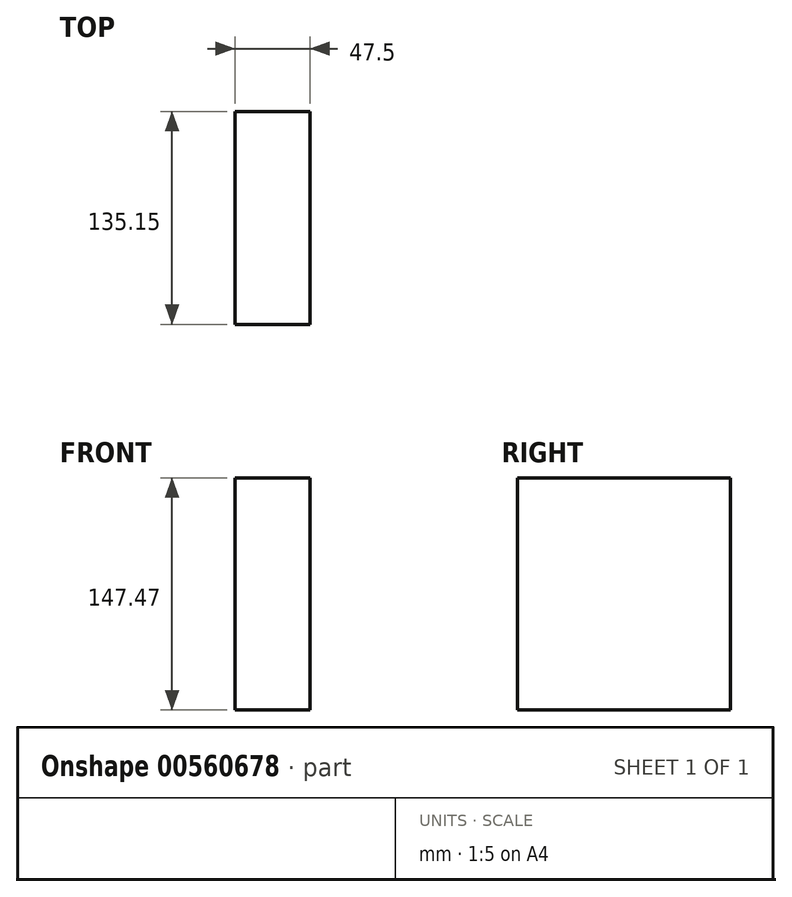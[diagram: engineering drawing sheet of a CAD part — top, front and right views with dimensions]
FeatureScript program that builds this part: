
annotation { "Feature Type Name" : "Feature", "Feature Type Description" : "" }
export const myFeature = defineFeature(function(context is Context, id is Id, definition is map)
    precondition{}
    {
        {
            var Q0;
            Q0=qCreatedBy(makeId("Right.planeOp"),FACE);
            var sketch = newSketch(context, id + "F0", { "sketchPlane" : qUnion([Q0])});
            skLineSegment(sketch, "E0.bottom", {"start": v(-32.49, 44.94) * mm, "end": v(102.66, 44.94) * mm});
            skLineSegment(sketch, "E0.top", {"start": v(-32.49, -102.53) * mm, "end": v(102.66, -102.53) * mm});
            skLineSegment(sketch, "E0.left", {"start": v(-32.49, 44.94) * mm, "end": v(-32.49, -102.53) * mm});
            skLineSegment(sketch, "E0.right", {"start": v(102.66, 44.94) * mm, "end": v(102.66, -102.53) * mm});
            skLineSegment(sketch, "E1.bottom", {"start": v(102.66, -102.53) * mm, "end": v(157.89, -102.53) * mm});
            skLineSegment(sketch, "E1.top", {"start": v(102.66, -130.9) * mm, "end": v(157.89, -130.9) * mm});
            skLineSegment(sketch, "E1.left", {"start": v(102.66, -102.53) * mm, "end": v(102.66, -130.9) * mm});
            skLineSegment(sketch, "E1.right", {"start": v(157.89, -102.53) * mm, "end": v(157.89, -130.9) * mm});
            skPoint(sketch, "E2.0", {"position": v(0, 0) * mm});
            skSolve(sketch);
        }
        {
            var Q0;
            Q0 = qSketchRegion(id + "F0", true);
            extrude(context, id + "F1", {"entities" : qUnion([Q0]), "depth" : 47.5 * mm, "offsetDistance" : 25.4 * mm});
        }
        {
            var Q0;
            Q0=makeQuery(id+"F1.opExtrude","SWEPT_BODY",BODY,{"disambiguationData":[OSD([sQuery(id+"F0.wireOp",EDGE,"E1.bottom"),sQuery(id+"F0.wireOp",EDGE,"E1.top"),sQuery(id+"F0.wireOp",EDGE,"E1.left"),sQuery(id+"F0.wireOp",EDGE,"E1.right")])]});
            deleteBodies(context, id + "F2", {"entities" : qUnion([Q0])});
        }
    });
